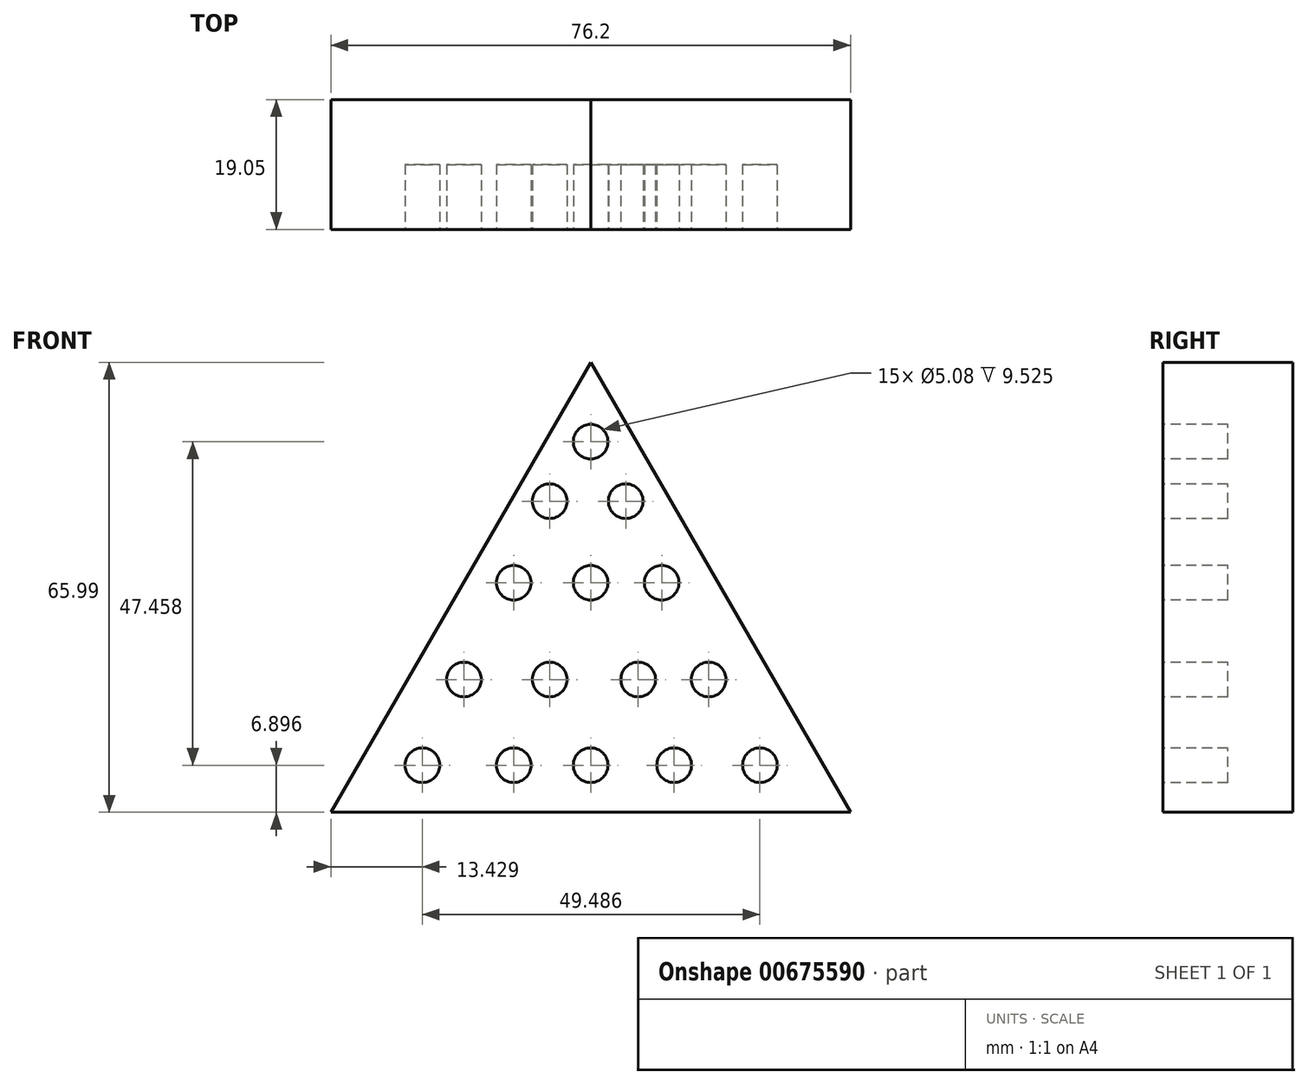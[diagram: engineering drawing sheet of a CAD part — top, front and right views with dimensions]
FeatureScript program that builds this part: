
annotation { "Feature Type Name" : "Feature", "Feature Type Description" : "" }
export const myFeature = defineFeature(function(context is Context, id is Id, definition is map)
    precondition{}
    {
        {
            var Q0;
            Q0=qCreatedBy(makeId("Front.planeOp"),FACE);
            var sketch = newSketch(context, id + "F0", { "sketchPlane" : qUnion([Q0])});
            skLineSegment(sketch, "E0", {"start": v(-76.2, 0) * mm, "end": v(-38.1, 66) * mm});
            skLineSegment(sketch, "E1", {"start": v(-38.1, 66) * mm, "end": v(0, 0) * mm});
            skLineSegment(sketch, "E2", {"start": v(0, 0) * mm, "end": v(-76.2, 0) * mm});
            skSolve(sketch);
        }
        {
            var Q0;
            Q0=makeQuery(id+"F0.imprint","IMPRINT",FACE,{"disambiguationData":[TD([[makeQuery(id+"F0.imprint","IMPRINT",EDGE,{"derivedFrom":sQuery(id+"F0.wireOp",EDGE,"E0")}),-1.0]])]});
            extrude(context, id + "F1", {"entities" : qUnion([Q0]), "depth" : 19.05 * mm, "offsetDistance" : 25.4 * mm});
        }
        {
            var Q0;
            Q0=makeQuery(id+"F1.opExtrude","CAP_FACE",FACE,{"disambiguationData":[OSD([sQuery(id+"F0.wireOp",EDGE,"E0"),sQuery(id+"F0.wireOp",EDGE,"E1"),sQuery(id+"F0.wireOp",EDGE,"E2")])],"isStart":false});
            var sketch = newSketch(context, id + "F2", { "sketchPlane" : qUnion([Q0])});
            skCircle(sketch, "E3", {"center": v(-38.1, 6.9) * mm, "radius": 2.54 * mm});
            skCircle(sketch, "E4", {"center": v(-62.77, 6.9) * mm, "radius": 2.54 * mm});
            skCircle(sketch, "E5", {"center": v(-49.39, 6.9) * mm, "radius": 2.54 * mm});
            skCircle(sketch, "E6", {"center": v(-25.86, 6.9) * mm, "radius": 2.54 * mm});
            skCircle(sketch, "E7", {"center": v(-13.28, 6.9) * mm, "radius": 2.54 * mm});
            skCircle(sketch, "E8", {"center": v(-56.69, 19.47) * mm, "radius": 2.54 * mm});
            skCircle(sketch, "E9", {"center": v(-44.11, 19.47) * mm, "radius": 2.54 * mm});
            skCircle(sketch, "E10", {"center": v(-31.13, 19.47) * mm, "radius": 2.54 * mm});
            skCircle(sketch, "E11", {"center": v(-20.79, 19.47) * mm, "radius": 2.54 * mm});
            skCircle(sketch, "E12", {"center": v(-38.1, 33.67) * mm, "radius": 2.54 * mm});
            skCircle(sketch, "E13", {"center": v(-49.39, 33.67) * mm, "radius": 2.54 * mm});
            skCircle(sketch, "E14", {"center": v(-27.68, 33.67) * mm, "radius": 2.54 * mm});
            skCircle(sketch, "E15", {"center": v(-44.11, 45.63) * mm, "radius": 2.54 * mm});
            skCircle(sketch, "E16", {"center": v(-38.1, 54.35) * mm, "radius": 2.54 * mm});
            skCircle(sketch, "E17", {"center": v(-32.96, 45.63) * mm, "radius": 2.54 * mm});
            skSolve(sketch);
        }
        {
            var Q0;
            Q0=makeQuery(id+"F2.imprint","IMPRINT",FACE,{"disambiguationData":[TD([[makeQuery(id+"F2.imprint","IMPRINT",EDGE,{"derivedFrom":sQuery(id+"F2.wireOp",EDGE,"E4")}),1.0]])]});
            extrude(context, id + "F3", {"entities" : qUnion([Q0]), "operationType" : NewBodyOperationType.REMOVE, "oppositeDirection" : true, "depth" : 9.52 * mm, "offsetDistance" : 25.4 * mm});
        }
        {
            var Q0;
            Q0 = qSketchRegion(id + "F2", true);
            extrude(context, id + "F4", {"entities" : qUnion([Q0]), "operationType" : NewBodyOperationType.REMOVE, "oppositeDirection" : true, "depth" : 9.52 * mm, "offsetDistance" : 25.4 * mm});
        }
    });
